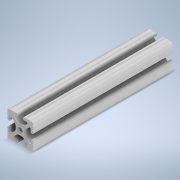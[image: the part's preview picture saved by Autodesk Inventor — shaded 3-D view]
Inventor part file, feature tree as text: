
AUTODESK INVENTOR PART (.ipt)
format: ipt  version: 2020 (Build 240168000, 168)  size: 249,344 bytes
history: native  units: in
note: dims shown in document units (in); Inventor stores cm internally (conversion verified against a paired STEP export)
features: extrude x1, sketch x1, other x1
ambient origin geometry x8: Origin, YZ Plane, XZ Plane, XY Plane, X Axis, Y Axis, Z Axis, Center Point
bodies: Solid1 (feature_tree)
feature tree (3):
  extrude  "Extrusion1"  [1 undecoded]
  sketch  "Sketch1"  dims[d0=28.0in d1=0.0in]
  other  "Boss-Extrude1"
note: 1 required parameter value undecoded (feature->parameter linkage not recoverable at this tier; creation-order binding heuristic only, values carry confidence <= 0.55)
